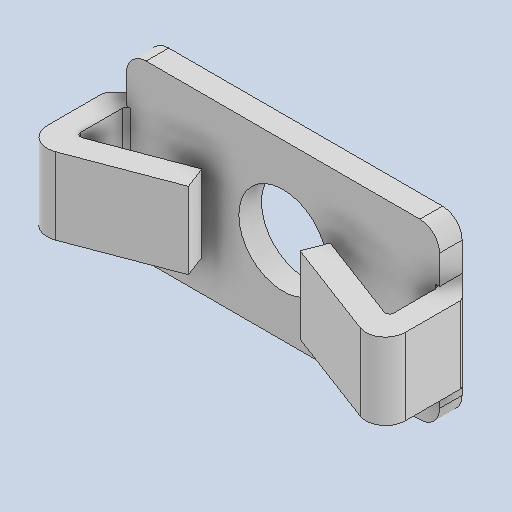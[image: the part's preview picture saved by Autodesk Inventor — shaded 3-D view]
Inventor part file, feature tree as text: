
AUTODESK INVENTOR PART (.ipt)
format: ipt  version: 2022 (Build 260153000, 153)  size: 128,000 bytes
history: native  units: in
note: dims shown in document units (in); Inventor stores cm internally (conversion verified against a paired STEP export)
features: fillet x1
ambient origin geometry x8: Origin, YZ Plane, XZ Plane, XY Plane, X Axis, Y Axis, Z Axis, Center Point
bodies: Solid1 (feature_tree)
feature tree (1):
  fillet  "Fillet7"  [1 undecoded]
note: 1 required parameter value undecoded (feature->parameter linkage not recoverable at this tier; creation-order binding heuristic only, values carry confidence <= 0.55)
